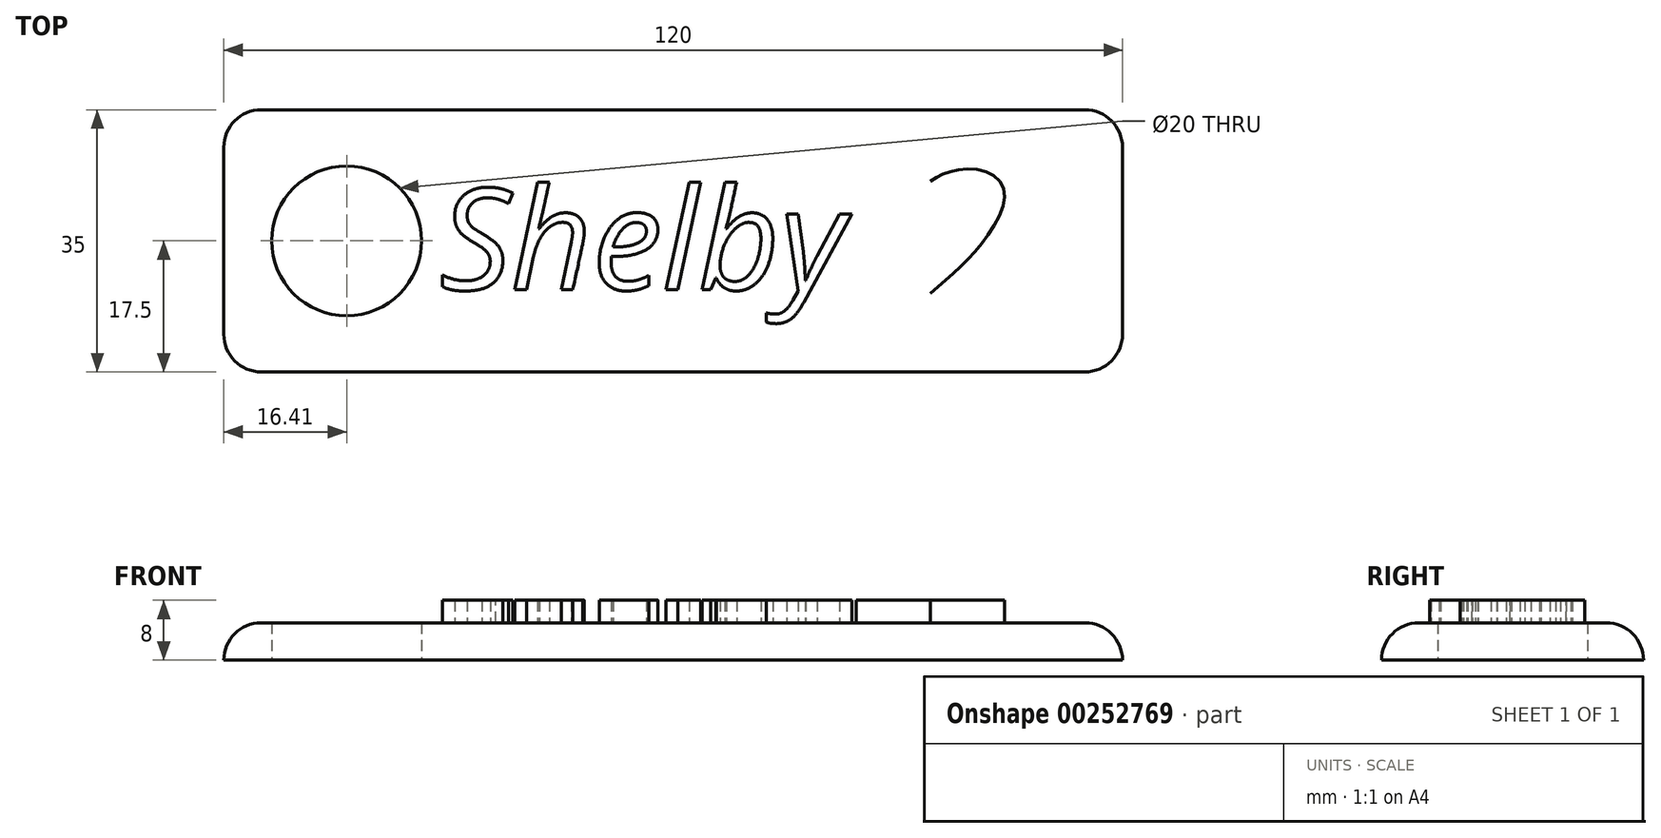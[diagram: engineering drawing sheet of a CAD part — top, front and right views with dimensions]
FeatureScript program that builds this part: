
annotation { "Feature Type Name" : "Feature", "Feature Type Description" : "" }
export const myFeature = defineFeature(function(context is Context, id is Id, definition is map)
    precondition{}
    {
        {
            var Q0;
            Q0=qCreatedBy(makeId("Top.planeOp"),FACE);
            var sketch = newSketch(context, id + "F0", { "sketchPlane" : qUnion([Q0])});
            skLineSegment(sketch, "E0.bottom", {"start": v(-60, 17.5) * mm, "end": v(60, 17.5) * mm});
            skLineSegment(sketch, "E0.top", {"start": v(-60, -17.5) * mm, "end": v(60, -17.5) * mm});
            skLineSegment(sketch, "E0.left", {"start": v(-60, 17.5) * mm, "end": v(-60, -17.5) * mm});
            skLineSegment(sketch, "E0.right", {"start": v(60, 17.5) * mm, "end": v(60, -17.5) * mm});
            skPoint(sketch, "E0.middle", {"position": v(0, 0) * mm});
            skCircle(sketch, "E1", {"center": v(-43.59, 0) * mm, "radius": 10 * mm});
            skSolve(sketch);
        }
        {
            var Q0;
            Q0=makeQuery(id+"F0.imprint","IMPRINT",FACE,{"disambiguationData":[TD([[makeQuery(id+"F0.imprint","IMPRINT",EDGE,{"derivedFrom":sQuery(id+"F0.wireOp",EDGE,"E0.bottom")}),-1.0]])]});
            extrude(context, id + "F1", {"entities" : qUnion([Q0]), "depth" : 5 * mm});
        }
        {
            var Q0;
            Q0=makeQuery(id+"F1.opExtrude","SWEPT_EDGE",EDGE,{"disambiguationData":[OSD([sQuery(id+"F0.wireOp",EDGE,"E0.top"),sQuery(id+"F0.wireOp",EDGE,"E0.left")])]});
            fillet(context, id + "F2", {"entities" : qUnion([Q0]), "radius" : 5 * mm, "tangentPropagation" : true, "allowEdgeOverflow" : false});
        }
        {
            var Q0;
            Q0=makeQuery(id+"F1.opExtrude","SWEPT_EDGE",EDGE,{"disambiguationData":[OSD([sQuery(id+"F0.wireOp",EDGE,"E0.bottom"),sQuery(id+"F0.wireOp",EDGE,"E0.left")])]});
            fillet(context, id + "F3", {"entities" : qUnion([Q0]), "radius" : 5 * mm, "tangentPropagation" : true, "allowEdgeOverflow" : false});
        }
        {
            var Q0;
            Q0=makeQuery(id+"F1.opExtrude","SWEPT_EDGE",EDGE,{"disambiguationData":[OSD([sQuery(id+"F0.wireOp",EDGE,"E0.bottom"),sQuery(id+"F0.wireOp",EDGE,"E0.right")])]});
            fillet(context, id + "F4", {"entities" : qUnion([Q0]), "radius" : 5 * mm, "tangentPropagation" : true, "allowEdgeOverflow" : false});
        }
        {
            var Q0;
            Q0=makeQuery(id+"F1.opExtrude","SWEPT_EDGE",EDGE,{"disambiguationData":[OSD([sQuery(id+"F0.wireOp",EDGE,"E0.top"),sQuery(id+"F0.wireOp",EDGE,"E0.right")])]});
            fillet(context, id + "F5", {"entities" : qUnion([Q0]), "radius" : 5 * mm, "tangentPropagation" : true, "allowEdgeOverflow" : false});
        }
        {
            var Q0;
            Q0=makeQuery(id+"F1.opExtrude","CAP_EDGE",EDGE,{"disambiguationData":[OSD([sQuery(id+"F0.wireOp",EDGE,"E0.left")])],"isStart":false});
            fillet(context, id + "F6", {"entities" : qUnion([Q0]), "radius" : 5 * mm, "tangentPropagation" : true, "allowEdgeOverflow" : false});
        }
        {
            var Q0;
            Q0=makeQuery(id+"F1.opExtrude","CAP_FACE",FACE,{"disambiguationData":[OSD([sQuery(id+"F0.wireOp",EDGE,"E0.bottom"),sQuery(id+"F0.wireOp",EDGE,"E0.top"),sQuery(id+"F0.wireOp",EDGE,"E0.left"),sQuery(id+"F0.wireOp",EDGE,"E0.right"),sQuery(id+"F0.wireOp",EDGE,"E1")])],"isStart":false});
            var sketch = newSketch(context, id + "F7", { "sketchPlane" : qUnion([Q0])});
            skText(sketch, "E2", { "text": "Shelby", "fontName": "OpenSans-Italic.ttf"});
            const initialGuessF7  = {"E2": [-0.03116, -0.00652, 1, 0, 0.0136]};
            skSetInitialGuess(sketch, initialGuessF7);
            skSolve(sketch);
        }
        {
            var Q0;
            Q0 = qSketchRegion(id + "F7", true);
            extrude(context, id + "F8", {"entities" : qUnion([Q0]), "operationType" : NewBodyOperationType.ADD, "depth" : 3 * mm});
        }
        {
            var Q0;
            {var subQ0=sQuery(id+"F0.wireOp",EDGE,"E0.left");var subQ1=sQuery(id+"F0.wireOp",EDGE,"E1");var subQ2=sQuery(id+"F0.wireOp",EDGE,"E0.right");var subQ3=sQuery(id+"F0.wireOp",EDGE,"E0.top");var subQ4=sQuery(id+"F0.wireOp",EDGE,"E0.bottom");var subQ5=makeQuery(id+"F1.opExtrude","CAP_FACE",FACE,{"disambiguationData":[OSD([subQ4,subQ3,subQ0,subQ2,subQ1])],"isStart":false});var subQ6=subQ5;var subQ7=subQ6;var subQ8=subQ7;Q0=makeQuery(id+"F8.boolean.opBoolean","SPLIT",FACE,{"disambiguationData":[TD([makeQuery(id+"F1.opExtrude","SWEPT_FACE",FACE,{"disambiguationData":[OSD([subQ1])]})])],"derivedFrom":subQ8});}
            var sketch = newSketch(context, id + "F9", { "sketchPlane" : qUnion([Q0])});
            skLineSegment(sketch, "E3", {"start": v(34.37, 16.42) * mm, "end": v(34.37, -22.32) * mm, "construction": true});
            skFitSpline(sketch, "E4", {"points": [v(34.37, 8) * mm, v(37.06, 9.27) * mm, v(41.52, 9.34) * mm, v(44.21, 6.79) * mm, v(42.58, 1.62) * mm, v(38.62, -3.2) * mm, v(34.37, -7.02) * mm], "startDerivative": vector(18.27, 10.83) * mm, "endDerivative": vector(-23.39, -20.08) * mm});
            skFitSpline(sketch, "E5.MirrorCS", {"points": [v(34.37, 8) * mm, v(31.68, 9.27) * mm, v(27.22, 9.34) * mm, v(24.52, 6.79) * mm, v(26.15, 1.62) * mm, v(30.12, -3.2) * mm, v(34.37, -7.02) * mm], "startDerivative": vector(-18.27, 10.83) * mm, "endDerivative": vector(23.39, -20.08) * mm});
            skSolve(sketch);
        }
        {
            var Q0;
            Q0 = qSketchRegion(id + "F9", true);
            extrude(context, id + "F10", {"entities" : qUnion([Q0]), "operationType" : NewBodyOperationType.ADD, "depth" : 3 * mm});
        }
    });
